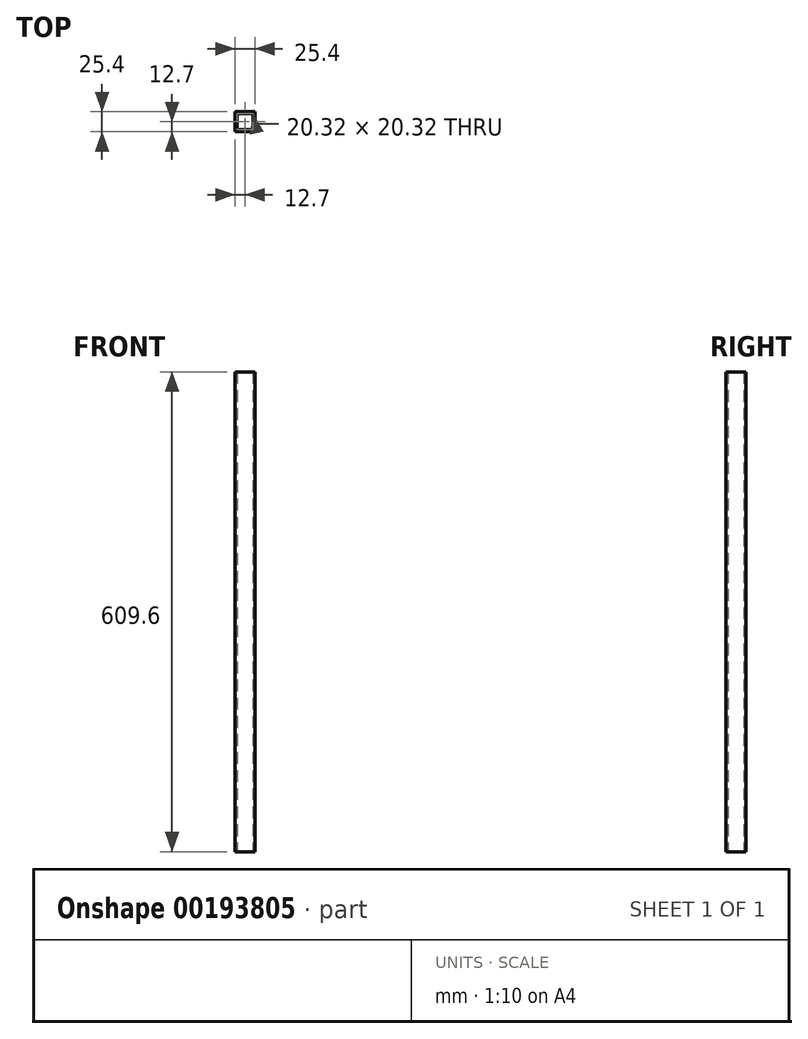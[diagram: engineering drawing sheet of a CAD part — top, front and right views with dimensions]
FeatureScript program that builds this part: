
annotation { "Feature Type Name" : "Feature", "Feature Type Description" : "" }
export const myFeature = defineFeature(function(context is Context, id is Id, definition is map)
    precondition{}
    {
        {
            var Q0;
            Q0=qCreatedBy(makeId("Top.planeOp"),FACE);
            var sketch = newSketch(context, id + "F0", { "sketchPlane" : qUnion([Q0])});
            skLineSegment(sketch, "E0.bottom", {"start": v(10.16, -10.16) * mm, "end": v(-10.16, -10.16) * mm});
            skLineSegment(sketch, "E0.top", {"start": v(10.16, 10.16) * mm, "end": v(-10.16, 10.16) * mm});
            skLineSegment(sketch, "E0.left", {"start": v(10.16, -10.16) * mm, "end": v(10.16, 10.16) * mm});
            skLineSegment(sketch, "E0.right", {"start": v(-10.16, -10.16) * mm, "end": v(-10.16, 10.16) * mm});
            skPoint(sketch, "E0.middle", {"position": v(0, 0) * mm});
            skLineSegment(sketch, "E1.bottom", {"start": v(12.7, -12.7) * mm, "end": v(-12.7, -12.7) * mm});
            skLineSegment(sketch, "E1.top", {"start": v(12.7, 12.7) * mm, "end": v(-12.7, 12.7) * mm});
            skLineSegment(sketch, "E1.left", {"start": v(12.7, -12.7) * mm, "end": v(12.7, 12.7) * mm});
            skLineSegment(sketch, "E1.right", {"start": v(-12.7, -12.7) * mm, "end": v(-12.7, 12.7) * mm});
            skSolve(sketch);
        }
        {
            var Q0;
            Q0=makeQuery(id+"F0.imprint","IMPRINT",FACE,{"disambiguationData":[TD([[makeQuery(id+"F0.imprint","IMPRINT",EDGE,{"derivedFrom":sQuery(id+"F0.wireOp",EDGE,"E0.bottom")}),1.0]])]});
            extrude(context, id + "F1", {"entities" : qUnion([Q0]), "depth" : 609.6 * mm});
        }
    });
